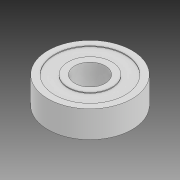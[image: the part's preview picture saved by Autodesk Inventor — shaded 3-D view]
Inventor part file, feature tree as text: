
AUTODESK INVENTOR PART (.ipt)
format: ipt  version: 2020 (Build 240168000, 168)  size: 112,640 bytes
history: native  units: mm
features: revolve x1, sketch x1
ambient origin geometry x8: Origin, YZ Plane, XZ Plane, XY Plane, X Axis, Y Axis, Z Axis, Center Point
bodies: Solid1 (feature_tree)
feature tree (2):
  revolve  "Revolution1"  [1 undecoded]
  sketch  "Sketch1"  dims[d0=4.0mm d1=11.0mm d2=7.0mm d3=0.2mm d4=3.5mm d5=90.0deg]
note: 1 required parameter value undecoded (feature->parameter linkage not recoverable at this tier; creation-order binding heuristic only, values carry confidence <= 0.55)
